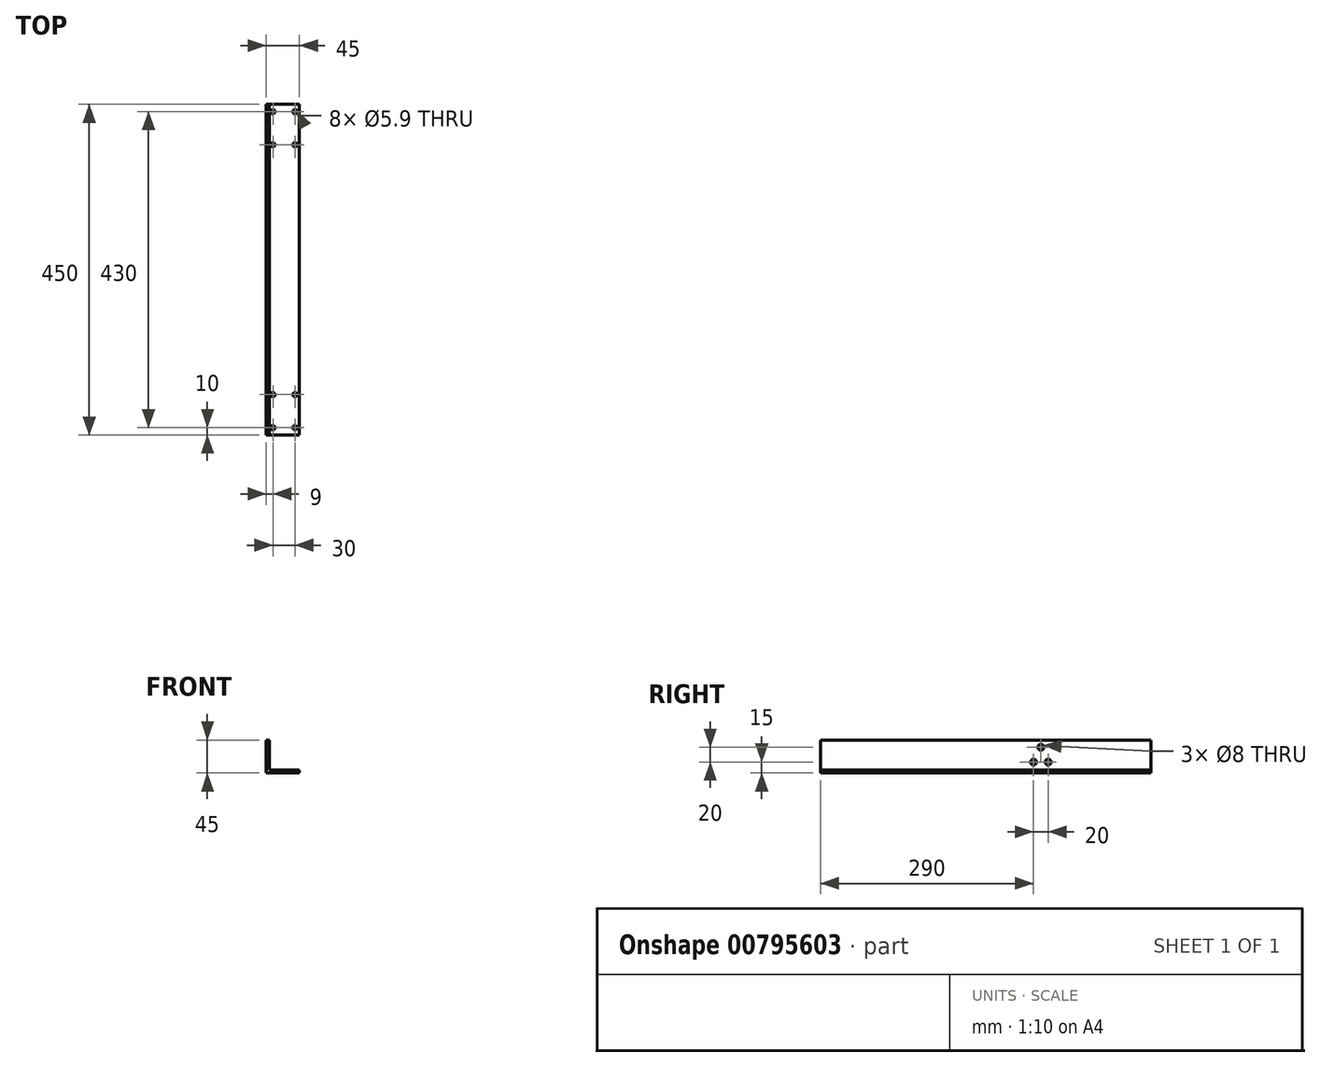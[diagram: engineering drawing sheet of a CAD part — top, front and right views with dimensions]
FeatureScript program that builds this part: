
annotation { "Feature Type Name" : "Feature", "Feature Type Description" : "" }
export const myFeature = defineFeature(function(context is Context, id is Id, definition is map)
    precondition{}
    {
        {
            var Q0;
            Q0=qCreatedBy(makeId("Front.planeOp"),FACE);
            var sketch = newSketch(context, id + "F0", { "sketchPlane" : qUnion([Q0])});
            skLineSegment(sketch, "E0.bottom", {"start": v(22.5, -22.5) * mm, "end": v(-22.5, -22.5) * mm});
            skLineSegment(sketch, "E0.top", {"start": v(-18.5, 22.5) * mm, "end": v(-22.5, 22.5) * mm});
            skLineSegment(sketch, "E0.left", {"start": v(22.5, -22.5) * mm, "end": v(22.5, -18.5) * mm});
            skLineSegment(sketch, "E0.right", {"start": v(-22.5, -22.5) * mm, "end": v(-22.5, 22.5) * mm});
            skPoint(sketch, "E0.middle", {"position": v(0, 0) * mm});
            skLineSegment(sketch, "E1", {"start": v(-18.5, 22.5) * mm, "end": v(-18.5, -18.5) * mm});
            skLineSegment(sketch, "E2", {"start": v(-18.5, -18.5) * mm, "end": v(22.5, -18.5) * mm});
            skSolve(sketch);
        }
        {
            var Q0;
            Q0=makeQuery(id+"F0.imprint","IMPRINT",FACE,{"disambiguationData":[TD([[makeQuery(id+"F0.imprint","IMPRINT",EDGE,{"derivedFrom":sQuery(id+"F0.wireOp",EDGE,"E0.bottom")}),-1.0]])]});
            extrude(context, id + "F1", {"entities" : qUnion([Q0]), "endBound" : BoundingType.SYMMETRIC, "depth" : 450 * mm, "offsetDistance" : 25 * mm});
        }
        {
            var Q0;
            Q0=makeQuery(id+"F1.opExtrude","SWEPT_FACE",FACE,{"disambiguationData":[OSD([sQuery(id+"F0.wireOp",EDGE,"E0.right")])]});
            var sketch = newSketch(context, id + "F2", { "sketchPlane" : qUnion([Q0])});
            skCircle(sketch, "E3", {"center": v(-75, 12.5) * mm, "radius": 4 * mm});
            skCircle(sketch, "E4", {"center": v(-85, -7.5) * mm, "radius": 4 * mm});
            skCircle(sketch, "E5", {"center": v(-65, -7.5) * mm, "radius": 4 * mm});
            skLineSegment(sketch, "E6", {"start": v(-85, -7.5) * mm, "end": v(-65, -7.5) * mm, "construction": true});
            skLineSegment(sketch, "E7", {"start": v(-75, -7.5) * mm, "end": v(-75, 12.5) * mm, "construction": true});
            skSolve(sketch);
        }
        {
            var Q0;
            Q0=sQuery(id+"F2.wireOp",VERTEX,"E7.end");
            var Q1;
            Q1=sQuery(id+"F2.wireOp",VERTEX,"E6.start");
            var Q2;
            Q2=sQuery(id+"F2.wireOp",VERTEX,"E6.end");
            var Q3;
            Q3=makeQuery(id+"F1.opExtrude","SWEPT_BODY",BODY,{"disambiguationData":[OSD([sQuery(id+"F0.wireOp",EDGE,"E0.bottom"),sQuery(id+"F0.wireOp",EDGE,"E0.top"),sQuery(id+"F0.wireOp",EDGE,"E0.left"),sQuery(id+"F0.wireOp",EDGE,"E0.right"),sQuery(id+"F0.wireOp",EDGE,"E1"),sQuery(id+"F0.wireOp",EDGE,"E2")])]});
            hole(context, id + "F3", {"style" : HoleStyle.SIMPLE, "endStyle" : HoleEndStyle.THROUGH, "standardTappedOrClearance" : lookupTablePath({ "standard" : "ISO", "size" : "8", "type" : "Drilled" }), "standardBlindInLast" : lookupTablePath({ "standard" : "ISO", "size" : "8", "type" : "Drilled" }), "holeDiameter" : 8 * mm, "majorDiameter" : 5 * mm, "isTappedThrough" : true, "tappedDepth" : 12.7 * mm, "tapClearance" : 3, "locations" : qUnion([Q0, Q1, Q2]), "scope" : qUnion([Q3])});
        }
        {
            var Q0;
            Q0=makeQuery(id+"F1.opExtrude","SWEPT_FACE",FACE,{"disambiguationData":[OSD([sQuery(id+"F0.wireOp",EDGE,"E2")])]});
            var sketch = newSketch(context, id + "F4", { "sketchPlane" : qUnion([Q0])});
            skLineSegment(sketch, "E8.bottom", {"start": v(-13.5, -170) * mm, "end": v(16.5, -170) * mm, "construction": true});
            skLineSegment(sketch, "E8.top", {"start": v(-13.5, -215) * mm, "end": v(16.5, -215) * mm, "construction": true});
            skLineSegment(sketch, "E8.left", {"start": v(-13.5, -170) * mm, "end": v(-13.5, -215) * mm, "construction": true});
            skLineSegment(sketch, "E8.right", {"start": v(16.5, -170) * mm, "end": v(16.5, -215) * mm, "construction": true});
            skLineSegment(sketch, "E9.bottom", {"start": v(-13.5, 215) * mm, "end": v(16.5, 215) * mm, "construction": true});
            skLineSegment(sketch, "E9.top", {"start": v(-13.5, 170) * mm, "end": v(16.5, 170) * mm, "construction": true});
            skLineSegment(sketch, "E9.left", {"start": v(-13.5, 215) * mm, "end": v(-13.5, 170) * mm, "construction": true});
            skLineSegment(sketch, "E9.right", {"start": v(16.5, 215) * mm, "end": v(16.5, 170) * mm, "construction": true});
            skSolve(sketch);
        }
        {
            var Q0;
            Q0=sQuery(id+"F4.wireOp",VERTEX,"E8.bottom.start");
            var Q1;
            Q1=sQuery(id+"F4.wireOp",VERTEX,"E8.bottom.end");
            var Q2;
            Q2=sQuery(id+"F4.wireOp",VERTEX,"E8.top.end");
            var Q3;
            Q3=sQuery(id+"F4.wireOp",VERTEX,"E8.top.start");
            var Q4;
            Q4=sQuery(id+"F4.wireOp",VERTEX,"E9.bottom.start");
            var Q5;
            Q5=sQuery(id+"F4.wireOp",VERTEX,"E9.bottom.end");
            var Q6;
            Q6=sQuery(id+"F4.wireOp",VERTEX,"E9.top.end");
            var Q7;
            Q7=sQuery(id+"F4.wireOp",VERTEX,"E9.top.start");
            var Q8;
            Q8=makeQuery(id+"F1.opExtrude","SWEPT_BODY",BODY,{"disambiguationData":[OSD([sQuery(id+"F0.wireOp",EDGE,"E0.bottom"),sQuery(id+"F0.wireOp",EDGE,"E0.top"),sQuery(id+"F0.wireOp",EDGE,"E0.left"),sQuery(id+"F0.wireOp",EDGE,"E0.right"),sQuery(id+"F0.wireOp",EDGE,"E1"),sQuery(id+"F0.wireOp",EDGE,"E2")])]});
            hole(context, id + "F5", {"style" : HoleStyle.SIMPLE, "endStyle" : HoleEndStyle.THROUGH, "holeDiameter" : 5.9 * mm, "majorDiameter" : 5 * mm, "isTappedThrough" : true, "tappedDepth" : 12.7 * mm, "tapClearance" : 3, "locations" : qUnion([Q0, Q1, Q2, Q3, Q4, Q5, Q6, Q7]), "scope" : qUnion([Q8])});
        }
    });
